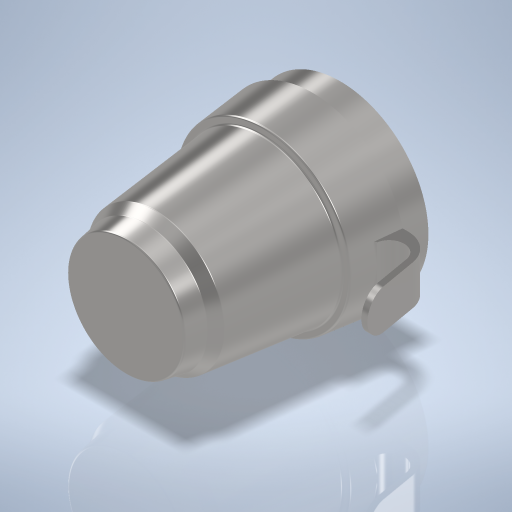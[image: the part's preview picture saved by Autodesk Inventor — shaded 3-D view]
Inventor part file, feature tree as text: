
AUTODESK INVENTOR PART (.ipt)
format: ipt  version: 2024 (Build 280153000, 153)  size: 476,160 bytes
history: native  units: mm
features: fillet x6, other x3, sketch x3, revolve x2, plane x1, extrude x1, shell x1, projected_geometry x1
ambient origin geometry x8: Origin, YZ Plane, XZ Plane, XY Plane, X Axis, Y Axis, Z Axis, Center Point
bodies: Volumenkörper1 (feature_tree)
feature tree (18):
  revolve  "Umdrehung1"
  plane  "Arbeitsebene1"
  revolve  "Umdrehung2"
  other  "Arbeitspunkt2"
  other  "Arbeitsachse4"
  extrude  "Extrusion2"  Depth=10.0mm
  fillet  "Rundung1"  Radius=95.0mm
  shell  "Wandung2"  Thickness=1.0mm
  fillet  "Rundung2"  Radius=110.0mm
  fillet  "Rundung3"  Radius=17.453293mm
  fillet  "Rundung4"  Radius=59.0mm
  fillet  "Rundung5"  Radius=69.0mm
  fillet  "Rundung6"  [1 undecoded]
  sketch  "Skizze1"  dims[d0=89.0mm d2=10.0mm d3=95.0mm d4=1.0mm d5=110.0mm d7=17.453293mm d8=59.0mm d9=69.0mm d10=90.0deg]
  sketch  "Skizze2"  dims[d11=0.0mm]
  other  "Arbeitsachse1"
  sketch  "Skizze6"  dims[d12=25.0mm d13=69.0mm d14=93.0mm d15=360.0deg d20=15.0mm d21=2.792527mm d22=16.0mm d26=3.0mm d27=40.0mm d31=7.5mm d33=20.0mm d34=0.0mm d35=10.0mm d37=1.0mm d38=1.0mm d39=1.0mm d40=1.0mm d41=1.0mm d42=1.0mm d43=1.0mm]
  projected_geometry  "Projizierte Kontur2"
note: 1 required parameter value undecoded (feature->parameter linkage not recoverable at this tier; creation-order binding heuristic only, values carry confidence <= 0.55)
